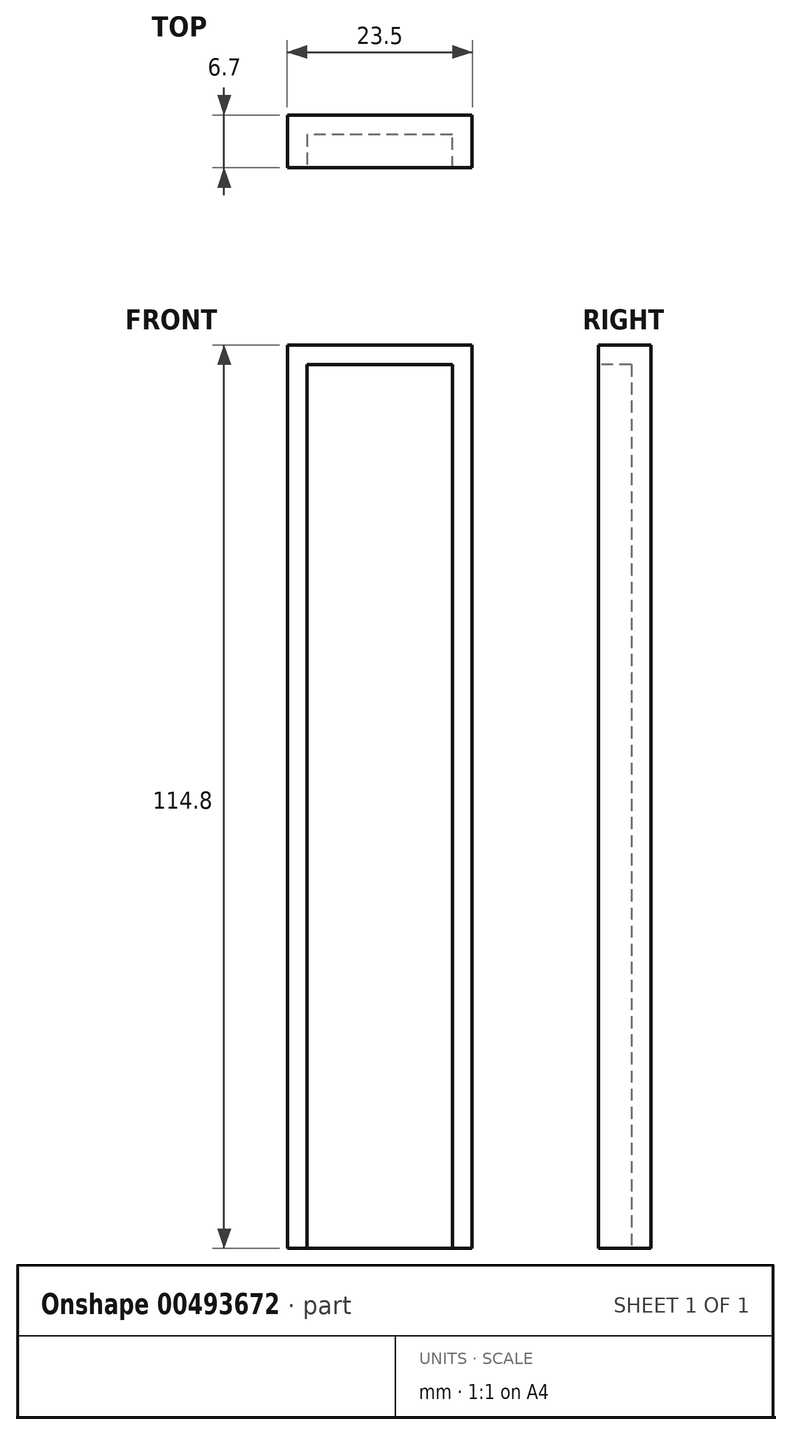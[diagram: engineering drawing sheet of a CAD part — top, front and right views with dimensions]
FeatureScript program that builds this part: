
annotation { "Feature Type Name" : "Feature", "Feature Type Description" : "" }
export const myFeature = defineFeature(function(context is Context, id is Id, definition is map)
    precondition{}
    {
        {
            var Q0;
            Q0=qCreatedBy(makeId("Front.planeOp"),FACE);
            var sketch = newSketch(context, id + "F0", { "sketchPlane" : qUnion([Q0])});
            skLineSegment(sketch, "E0.bottom", {"start": v(11.75, 58.9) * mm, "end": v(-11.74, 58.9) * mm});
            skLineSegment(sketch, "E0.top", {"start": v(11.75, -58.9) * mm, "end": v(-11.74, -58.9) * mm});
            skLineSegment(sketch, "E0.left", {"start": v(11.75, 58.9) * mm, "end": v(11.75, -58.9) * mm});
            skLineSegment(sketch, "E0.right", {"start": v(-11.74, 58.9) * mm, "end": v(-11.74, -58.9) * mm});
            skPoint(sketch, "E0.middle", {"position": v(0, 0) * mm});
            skSolve(sketch);
        }
        {
            var Q0;
            Q0=makeQuery(id+"F0.imprint","IMPRINT",FACE,{"disambiguationData":[TD([[makeQuery(id+"F0.imprint","IMPRINT",EDGE,{"derivedFrom":sQuery(id+"F0.wireOp",EDGE,"E0.bottom")}),1.0]])]});
            extrude(context, id + "F1", {"entities" : qUnion([Q0]), "oppositeDirection" : true, "depth" : 6.7 * mm});
        }
        {
            var Q0;
            Q0=makeQuery(id+"F1.opExtrude","CAP_FACE",FACE,{"disambiguationData":[OSD([sQuery(id+"F0.wireOp",EDGE,"E0.bottom"),sQuery(id+"F0.wireOp",EDGE,"E0.top"),sQuery(id+"F0.wireOp",EDGE,"E0.left"),sQuery(id+"F0.wireOp",EDGE,"E0.right")])],"isStart":true});
            shell(context, id + "F2", {"entities" : qUnion([Q0]), "thickness" : 2.5 * mm});
        }
        {
            var Q0;
            Q0=makeQuery(id+"F1.opExtrude","SWEPT_FACE",FACE,{"disambiguationData":[OSD([sQuery(id+"F0.wireOp",EDGE,"E0.top")])]});
            extrude(context, id + "F3", {"entities" : qUnion([Q0]), "operationType" : NewBodyOperationType.REMOVE, "oppositeDirection" : true, "depth" : 3 * mm});
        }
    });
